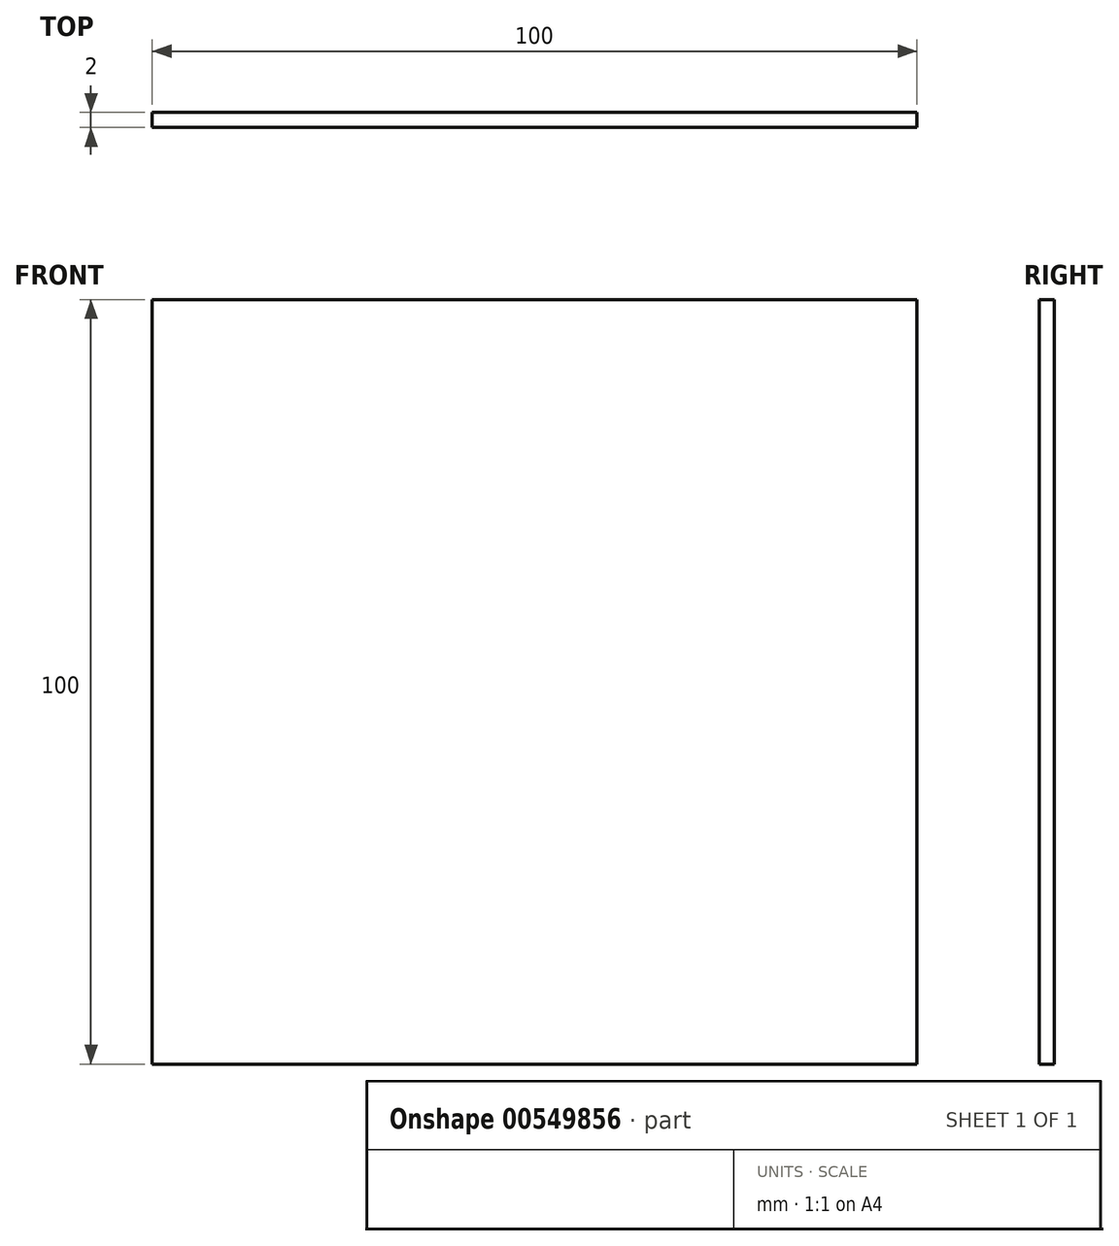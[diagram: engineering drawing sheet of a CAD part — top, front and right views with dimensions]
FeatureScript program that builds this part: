
annotation { "Feature Type Name" : "Feature", "Feature Type Description" : "" }
export const myFeature = defineFeature(function(context is Context, id is Id, definition is map)
    precondition{}
    {
        {
            var Q0;
            Q0=qCreatedBy(makeId("Front.planeOp"),FACE);
            var sketch = newSketch(context, id + "F0", { "sketchPlane" : qUnion([Q0])});
            skLineSegment(sketch, "E0.bottom", {"start": v(0, 0) * mm, "end": v(100, 0) * mm});
            skLineSegment(sketch, "E0.top", {"start": v(0, 100) * mm, "end": v(100, 100) * mm});
            skLineSegment(sketch, "E0.left", {"start": v(0, 0) * mm, "end": v(0, 100) * mm});
            skLineSegment(sketch, "E0.right", {"start": v(100, 0) * mm, "end": v(100, 100) * mm});
            skSolve(sketch);
        }
        {
            var Q0;
            Q0=makeQuery(id+"F0.imprint","IMPRINT",FACE,{"disambiguationData":[TD([[makeQuery(id+"F0.imprint","IMPRINT",EDGE,{"derivedFrom":sQuery(id+"F0.wireOp",EDGE,"E0.bottom")}),1.0]])]});
            extrude(context, id + "F1", {"entities" : qUnion([Q0]), "depth" : 2 * mm, "offsetDistance" : 25 * mm});
        }
    });
